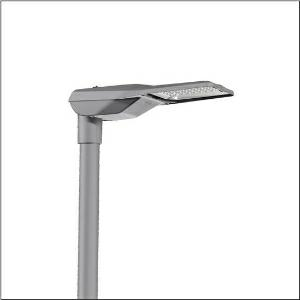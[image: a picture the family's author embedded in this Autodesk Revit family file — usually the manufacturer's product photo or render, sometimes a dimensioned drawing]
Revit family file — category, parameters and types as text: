
# Revit family: streetlight_sl_21_mini___p0_8ab_5xe2r33s08hb_da28
name_source: partatom
category: Lighting Fixtures
units: mm (PartAtom-declared; Revit-internal decimal feet)

## family parameters
Cut with Voids When Loaded = No
Host = Face
Light Source = No
Part Type = Normal
Room Calculation Point = No
Round Connector Dimension = Use Diameter
Shared = No

## types (1)
- --- (1 x LED, 7850 lm, 66 W, 3000K)
    Apparent Load = 66 VA
    CIE Flux Codes = 36 71 98 100 100
    Color Rendering = 70
    Color Temperature = 3000K
    Default Elevation = 1800 mm
    Description = Streetlight SL 21 mini, mast luminaire, primary light control with lens, of PMMA, primary optical cover: cover, of toughened safety glass, transparent, light distribution: P0.8aB, light emission: direct distribution, primary light characteristic: asymmetric, installation type: post-top, side-entry, LED, High Power LED, rated luminous flux: 7.850lm, luminous efficacy: 119lm/W, light colour: 730, colour temperature: 3000K, control gear: D4i, control: pre-setting: logarithmic dimming characteristic, flexible luminous flux parameterisation, time-dependent luminous flux control, constant luminous flux control, overheat protection, mains connection: 220..240V, AC, 50/60Hz, start of lifetime: 66W, end of service life: 69W, reduction: 30W, luminaire housing, of diecast aluminium, powder-coated, Siteco® metallic grey (DB 702S), corrosivity category C5 mid according to DIN EN ISO 12944, multi-level sealing system, sealing non-destructively replaceable, inclination adjustable: 0°, 5°, 10°, 15°, please order mast flange separately, length: 628mm, width: 235mm, height: 110mm, mast flange for spigot size: 42mm (side-entry): 5XC10008XM4, 60/48mm (side-entry/post-top): 5XC10108XM2, 76/60mm (side-entry/post-top): 5XC10108XM1, mounting height: 4..8m, Smart Interface above, protection rating (complete): IP66, insulation class (complete): insulation class II (safety insulation), certification: CE, ENEC, ENEC+, VDE, impact resistance: IK10, permissible operating ambient temperature for outdoor applications: -40..+50°C, standard-compliant lighting for roads and squares, packaging unit: 1 piece

Light Distribution: P0.8aB
    Height = 110 mm
    Lamp = 1 x LED
    Lamp Light Flux = 7850 lm
    Lamp Power = 66 W
    Lamp count = 1
    Length = 625 mm
    Luminous efficacy = 119 lm/W
    Manufacturer = Siteco
    ModVariant = No
    Model = 5XE2R33S08HB
    Number of Poles = 1
    OnlyDefault = Yes
    Power Factor = 1
    Product Name = Streetlight SL 21 mini | P0.8aB
    Product group = mast luminaire | pylon top
    ProductGroupID = 6100
    Protection Class = Protection class II
    Protection Degree = IP 66
    RLX_Detail_Level = 1
    RLX_Emergency_Light_Flux = 0 lm
    RLX_Emergency_Type = 0
    RLX_Emergency_Type_DB = No
    RlxData = <blob elided: 91661 chars, md5=86aedf22>
    Socket = socket
    Standby Power = 0 W
    System Light Flux = 7850 lm
    System Power = 66 W
    Type Comments = factory setting: luminous flux: 100 % | dim-lin: 254 | 670 mA
    Type Image = l_1003515.jpg
    URL = http://relux.com
    VarID = @adj_096419
    Voltage = 0 V
    Weight = 0.00 kg
    Width = 234 mm

## geometry (parser evidence)
native form markers: Blend x4, Sweep x11
no freeform markers — native parametric forms only
